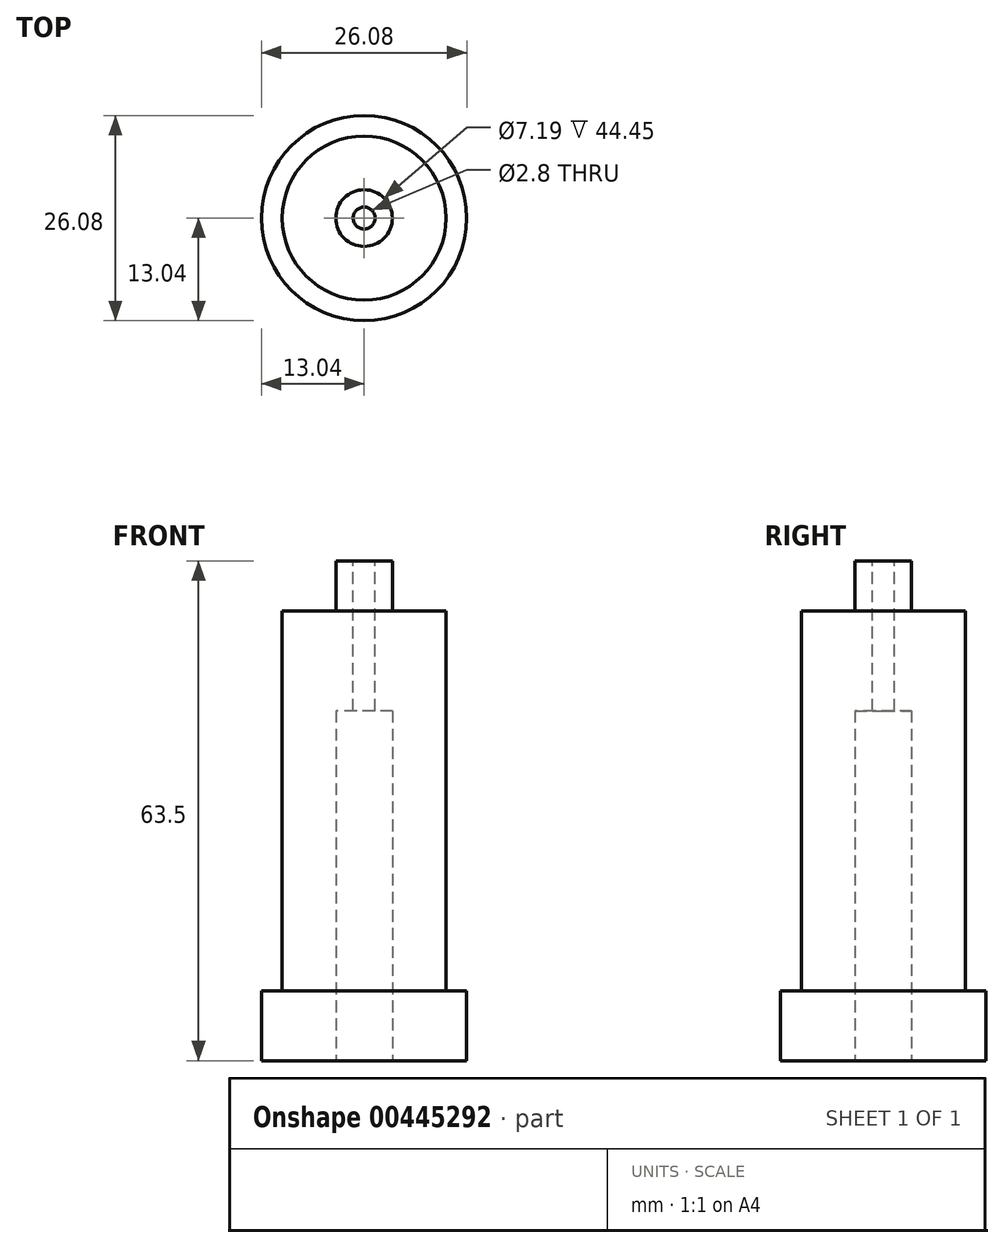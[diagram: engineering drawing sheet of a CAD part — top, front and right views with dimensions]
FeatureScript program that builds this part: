
annotation { "Feature Type Name" : "Feature", "Feature Type Description" : "" }
export const myFeature = defineFeature(function(context is Context, id is Id, definition is map)
    precondition{}
    {
        {
            var Q0;
            Q0=qCreatedBy(makeId("Top.planeOp"),FACE);
            var sketch = newSketch(context, id + "F0", { "sketchPlane" : qUnion([Q0])});
            skCircle(sketch, "E0", {"center": v(0, 0) * mm, "radius": 10.41 * mm});
            skCircle(sketch, "E1", {"center": v(0, 0) * mm, "radius": 13.04 * mm});
            skCircle(sketch, "E2", {"center": v(0, 0) * mm, "radius": 3.6 * mm});
            skSolve(sketch);
        }
        {
            var Q0;
            Q0=makeQuery(id+"F0.imprint","IMPRINT",FACE,{"disambiguationData":[TD([[makeQuery(id+"F0.imprint","IMPRINT",EDGE,{"derivedFrom":sQuery(id+"F0.wireOp",EDGE,"E0")}),-1.0]])]});
            var Q1;
            Q1=makeQuery(id+"F0.imprint","IMPRINT",FACE,{"disambiguationData":[TD([[makeQuery(id+"F0.imprint","IMPRINT",EDGE,{"derivedFrom":sQuery(id+"F0.wireOp",EDGE,"E0")}),1.0]])]});
            var Q2;
            Q2=makeQuery(id+"F0.imprint","IMPRINT",FACE,{"disambiguationData":[TD([[makeQuery(id+"F0.imprint","IMPRINT",EDGE,{"derivedFrom":sQuery(id+"F0.wireOp",EDGE,"E2")}),1.0]])]});
            extrude(context, id + "F1", {"entities" : qUnion([Q0, Q1, Q2]), "depth" : 12.7 * mm});
        }
        {
            var Q0;
            Q0=makeQuery(id+"F0.imprint","IMPRINT",FACE,{"disambiguationData":[TD([[makeQuery(id+"F0.imprint","IMPRINT",EDGE,{"derivedFrom":sQuery(id+"F0.wireOp",EDGE,"E0")}),1.0]])]});
            extrude(context, id + "F2", {"entities" : qUnion([Q0]), "operationType" : NewBodyOperationType.ADD, "depth" : 57.15 * mm});
        }
        {
            var Q0;
            Q0=makeQuery(id+"F2.boolean.opBoolean","SPLIT",FACE,{"disambiguationData":[TD([makeQuery(id+"F2.opExtrude","SWEPT_FACE",FACE,{"disambiguationData":[OSD([sQuery(id+"F0.wireOp",EDGE,"E2")])]})])],"derivedFrom":makeQuery(id+"F1.opExtrude","CAP_FACE",FACE,{"disambiguationData":[OSD([sQuery(id+"F0.wireOp",EDGE,"E1")])],"isStart":false})});
            extrude(context, id + "F3", {"entities" : qUnion([Q0]), "operationType" : NewBodyOperationType.ADD, "depth" : 50.8 * mm});
        }
        {
            var Q0;
            {var subQ0=sQuery(id+"F0.wireOp",EDGE,"E1");Q0=makeQuery(id+"F2.boolean.opBoolean","SPLIT",FACE,{"disambiguationData":[TD([makeQuery(id+"F1.opExtrude","SWEPT_FACE",FACE,{"disambiguationData":[OSD([subQ0])]})])],"derivedFrom":makeQuery(id+"F1.opExtrude","CAP_FACE",FACE,{"disambiguationData":[OSD([subQ0])],"isStart":false})});}
            extrude(context, id + "F4", {"entities" : qUnion([Q0]), "operationType" : NewBodyOperationType.REMOVE, "oppositeDirection" : true, "depth" : 3.8 * mm});
        }
        {
            var Q0;
            Q0=makeQuery(id+"F0.imprint","IMPRINT",FACE,{"disambiguationData":[TD([[makeQuery(id+"F0.imprint","IMPRINT",EDGE,{"derivedFrom":sQuery(id+"F0.wireOp",EDGE,"E2")}),1.0]])]});
            extrude(context, id + "F5", {"entities" : qUnion([Q0]), "operationType" : NewBodyOperationType.REMOVE, "depth" : 44.45 * mm});
        }
        {
            var Q0;
            Q0=makeQuery(id+"F3.opExtrude","CAP_FACE",FACE,{"disambiguationData":[OSD([sQuery(id+"F0.wireOp",EDGE,"E1")])],"isStart":false});
            var sketch = newSketch(context, id + "F6", { "sketchPlane" : qUnion([Q0])});
            skCircle(sketch, "E3", {"center": v(0, 0) * mm, "radius": 1.4 * mm});
            skSolve(sketch);
        }
        {
            var Q0;
            Q0=makeQuery(id+"F6.imprint","IMPRINT",FACE,{"disambiguationData":[TD([[makeQuery(id+"F6.imprint","IMPRINT",EDGE,{"derivedFrom":sQuery(id+"F6.wireOp",EDGE,"E3")}),1.0]])]});
            extrude(context, id + "F7", {"entities" : qUnion([Q0]), "operationType" : NewBodyOperationType.REMOVE, "endBound" : BoundingType.THROUGH_ALL, "oppositeDirection" : true, "depth" : 25.4 * mm});
        }
    });
